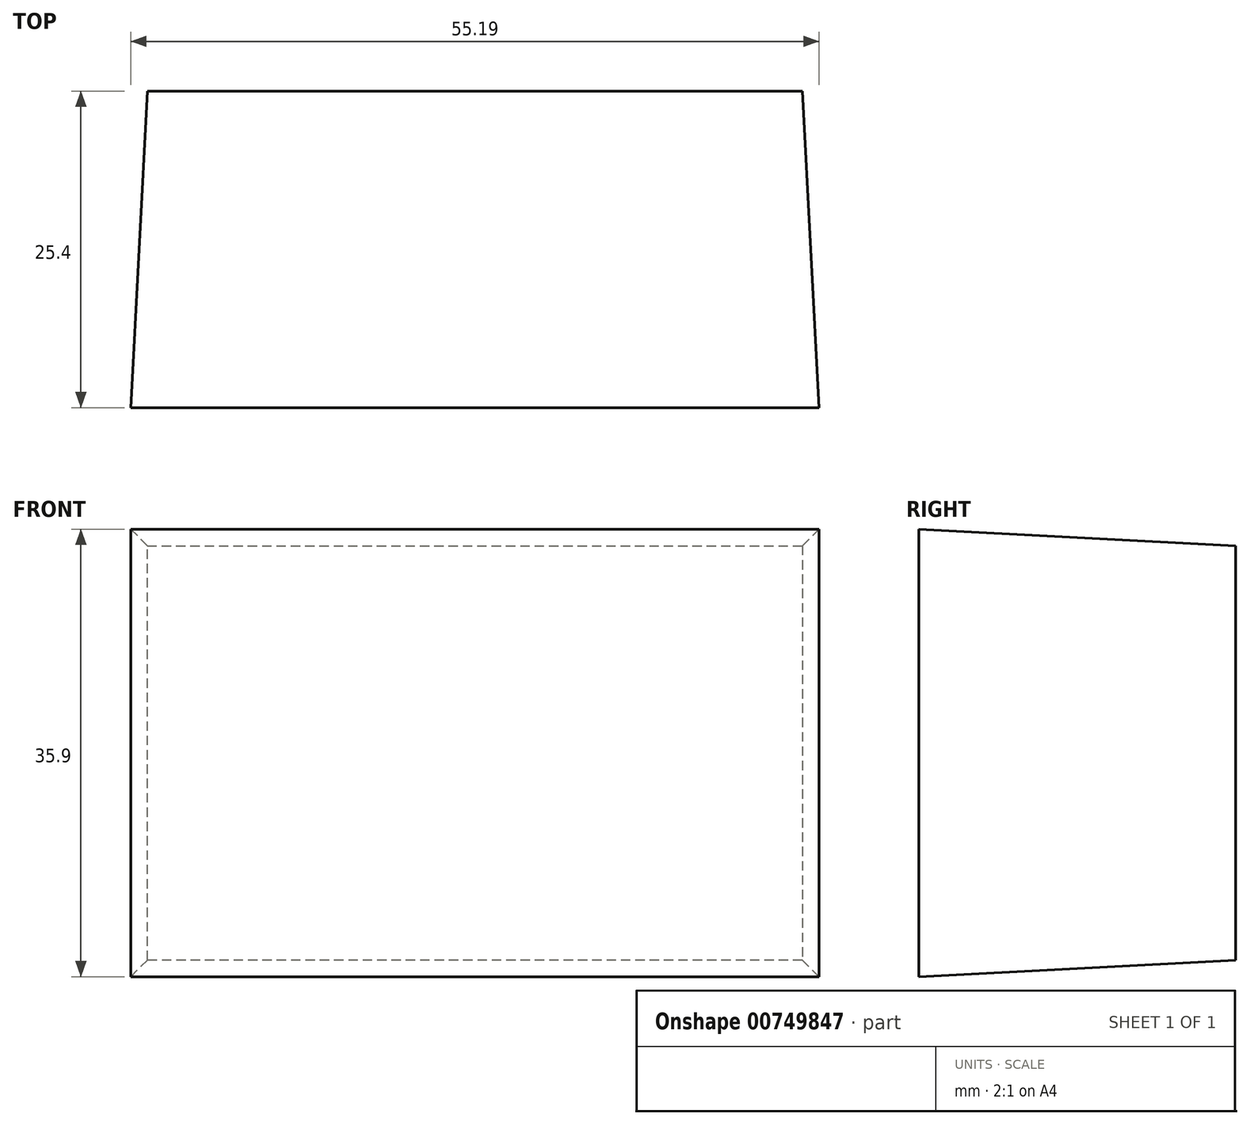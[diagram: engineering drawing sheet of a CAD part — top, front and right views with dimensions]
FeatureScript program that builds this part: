
annotation { "Feature Type Name" : "Feature", "Feature Type Description" : "" }
export const myFeature = defineFeature(function(context is Context, id is Id, definition is map)
    precondition{}
    {
        {
            var Q0;
            Q0=qCreatedBy(makeId("Front.planeOp"),FACE);
            var sketch = newSketch(context, id + "F0", { "sketchPlane" : qUnion([Q0])});
            skLineSegment(sketch, "E0.bottom", {"start": v(0, 0) * mm, "end": v(52.52, 0) * mm});
            skLineSegment(sketch, "E0.top", {"start": v(0, 33.24) * mm, "end": v(52.52, 33.24) * mm});
            skLineSegment(sketch, "E0.left", {"start": v(0, 0) * mm, "end": v(0, 33.24) * mm});
            skLineSegment(sketch, "E0.right", {"start": v(52.52, 0) * mm, "end": v(52.52, 33.24) * mm});
            skSolve(sketch);
        }
        {
            var Q0;
            Q0 = qSketchRegion(id + "F0", true);
            extrude(context, id + "F1", {"entities" : qUnion([Q0]), "depth" : 25.4 * mm, "offsetDistance" : 25.4 * mm, "hasDraft" : true, "draftAngle" : 3 * degree});
        }
    });
